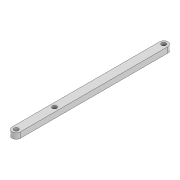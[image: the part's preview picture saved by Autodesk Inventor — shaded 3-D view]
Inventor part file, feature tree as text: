
AUTODESK INVENTOR PART (.ipt)
format: ipt  version: 2022 (Build 260153000, 153)  size: 87,040 bytes
history: native  units: mm
features: extrude x1, sketch x1
ambient origin geometry x8: Origin, YZ Plane, XZ Plane, XY Plane, X Axis, Y Axis, Z Axis, Center Point
bodies: Solid1 (feature_tree)
feature tree (2):
  extrude  "Extrusion1"  Depth=4.0mm
  sketch  "Sketch1"  dims[d0=3.2mm d1=3.2mm d2=6.0mm d3=105.413mm d4=3.2mm d5=27.392mm d6=4.0mm d7=0.0mm]
